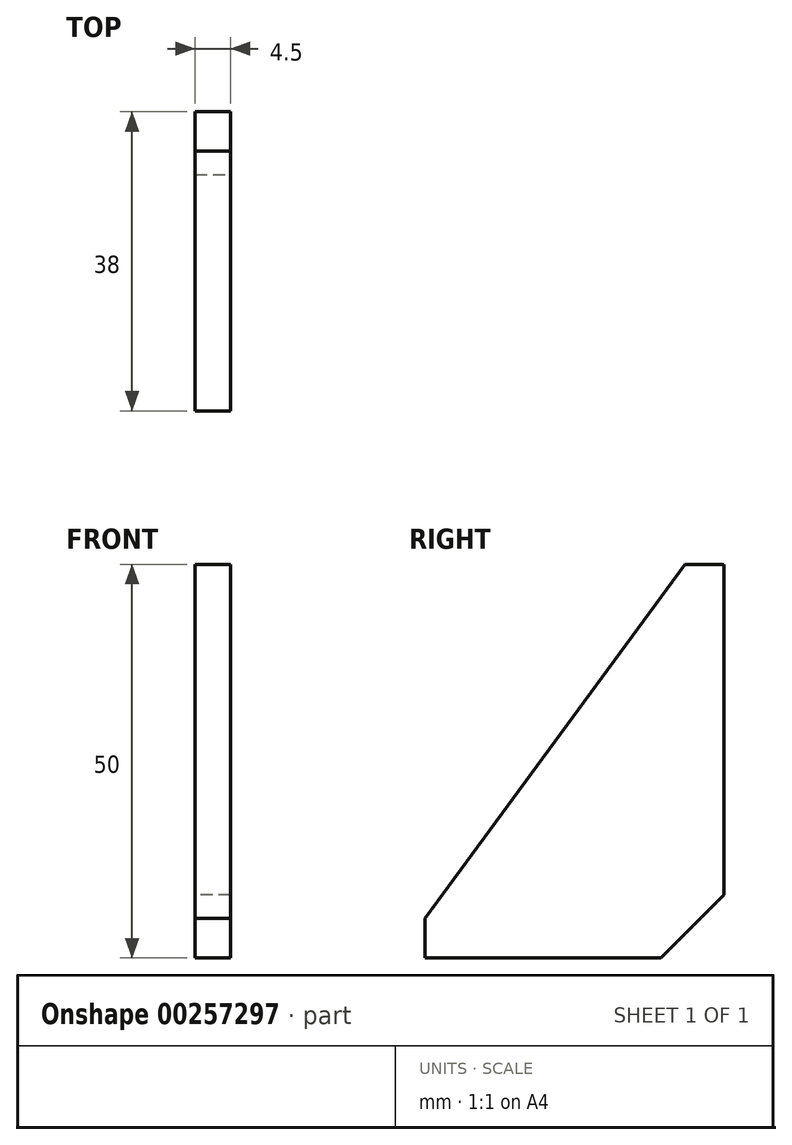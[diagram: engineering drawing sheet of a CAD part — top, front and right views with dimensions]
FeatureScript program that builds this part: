
annotation { "Feature Type Name" : "Feature", "Feature Type Description" : "" }
export const myFeature = defineFeature(function(context is Context, id is Id, definition is map)
    precondition{}
    {
        {
            var Q0;
            Q0=qCreatedBy(makeId("Right.planeOp"),FACE);
            var sketch = newSketch(context, id + "F0", { "sketchPlane" : qUnion([Q0])});
            skLineSegment(sketch, "E0", {"start": v(0, 0) * mm, "end": v(-38, 0) * mm});
            skLineSegment(sketch, "E1", {"start": v(-38, 0) * mm, "end": v(-38, 5) * mm});
            skLineSegment(sketch, "E2", {"start": v(-38, 5) * mm, "end": v(-5, 50) * mm});
            skLineSegment(sketch, "E3", {"start": v(-5, 50) * mm, "end": v(0, 50) * mm});
            skLineSegment(sketch, "E4", {"start": v(0, 50) * mm, "end": v(0, 0) * mm});
            skSolve(sketch);
        }
        {
            var Q0;
            Q0=makeQuery(id+"F0.imprint","IMPRINT",FACE,{"disambiguationData":[TD([[makeQuery(id+"F0.imprint","IMPRINT",EDGE,{"derivedFrom":sQuery(id+"F0.wireOp",EDGE,"E0")}),-1.0]])]});
            extrude(context, id + "F1", {"entities" : qUnion([Q0]), "oppositeDirection" : true, "depth" : 4.5 * mm});
        }
        {
            var Q0;
            Q0=makeQuery(id+"F1.opExtrude","SWEPT_EDGE",EDGE,{"disambiguationData":[OSD([sQuery(id+"F0.wireOp",EDGE,"E0"),sQuery(id+"F0.wireOp",EDGE,"E4")])]});
            chamfer(context, id + "F2", {"entities" : qUnion([Q0]), "width" : 8 * mm, "tangentPropagation" : true});
        }
    });
